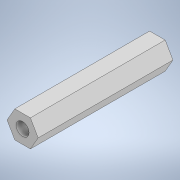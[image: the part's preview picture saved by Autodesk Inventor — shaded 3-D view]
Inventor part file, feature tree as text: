
AUTODESK INVENTOR PART (.ipt)
format: ipt  version: 2022.2 (Build 262287010, 287A)  size: 115,712 bytes
history: native  units: in
note: dims shown in document units (in); Inventor stores cm internally (conversion verified against a paired STEP export)
features: sketch x3, hole x2, extrude x1
ambient origin geometry x8: Origin, YZ Plane, XZ Plane, XY Plane, X Axis, Y Axis, Z Axis, Center Point
bodies: Body1 (feature_tree)
feature tree (6):
  extrude  "Extrusion2"  Depth=0.5in
  hole  "Hole1"  [1 undecoded]
  hole  "Hole2"  [1 undecoded]
  sketch  "Sketch1"  dims[d0=0.5in d3=0.159in]
  sketch  "Sketch2"  dims[d4=2.5in d5=0.0in]
  sketch  "Sketch3"  dims[d6=0.23in d7=0.75in d8=0.24in d9=0.2411in d10=0.5635in d11=0.31in d12=0.0in d13=0.23in d14=0.75in d15=0.24in d16=0.2411in d17=0.5635in d18=0.31in d19=0.0in]
note: 2 required parameter values undecoded (feature->parameter linkage not recoverable at this tier; creation-order binding heuristic only, values carry confidence <= 0.55)
